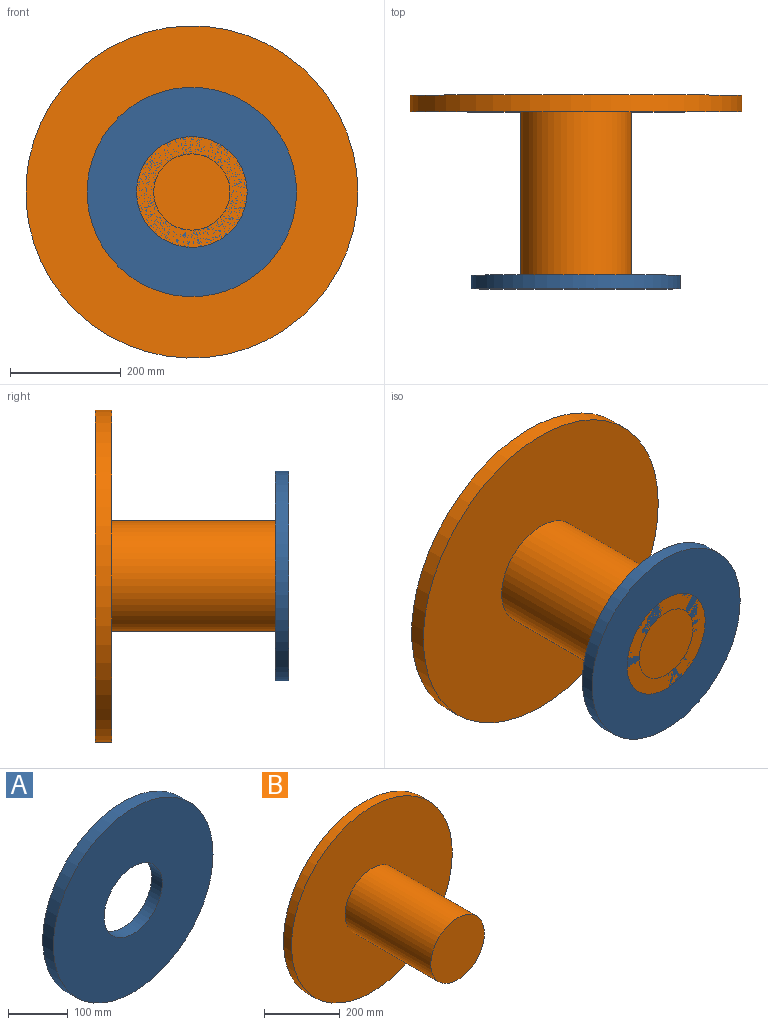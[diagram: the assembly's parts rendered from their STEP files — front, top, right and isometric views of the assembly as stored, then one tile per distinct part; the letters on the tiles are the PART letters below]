
ASSEMBLY  parts=2 mates=2
PART A: 4 faces, bbox 378.3x25x378.3 mm
  f0: cylinder r=68.86mm len=137.72mm, axis (0,1,0), area 10816.4mm2, adj f2,f3
  f1: cylinder r=189.14mm len=378.28mm, axis (0,1,0), area 29710.2mm2, adj f2,f3
  f2: plane 378.28x378.28mm, normal (0,-1,0), area 97492.5mm2, adj f0,f1
  f3: plane 378.28x378.28mm, normal (0,1,0), area 97492.5mm2, adj f0,f1
PART B: 5 faces, bbox 600x350x600 mm
  f0: cylinder r=300mm len=600mm, axis (0,1,0), area 56548.7mm2, adj f1,f2
  f1: plane 600x600mm, normal (0,-1,0), area 251327.4mm2, adj f0,f3
  f2: plane 600x600mm, normal (0,1,0), area 282743.3mm2, adj f0
  f3: cylinder r=100mm len=320mm, axis (0,1,0), area 201061.9mm2, adj f1,f4
  f4: plane 200x200mm, normal (0,-1,0), area 31415.9mm2, adj f3
PLACE A t=(585.65,139.47,33.13)mm
PLACE B t=(67.32,114.47,8.6)mm
MATE revolute B.f3 <-> B.f0  axis (0,-1,0) through (67.32,-235.53,8.6)mm
MATE fastened A.f0 <-> B.f3  axis (0,-1,0) through (67.32,-235.53,8.6)mm
